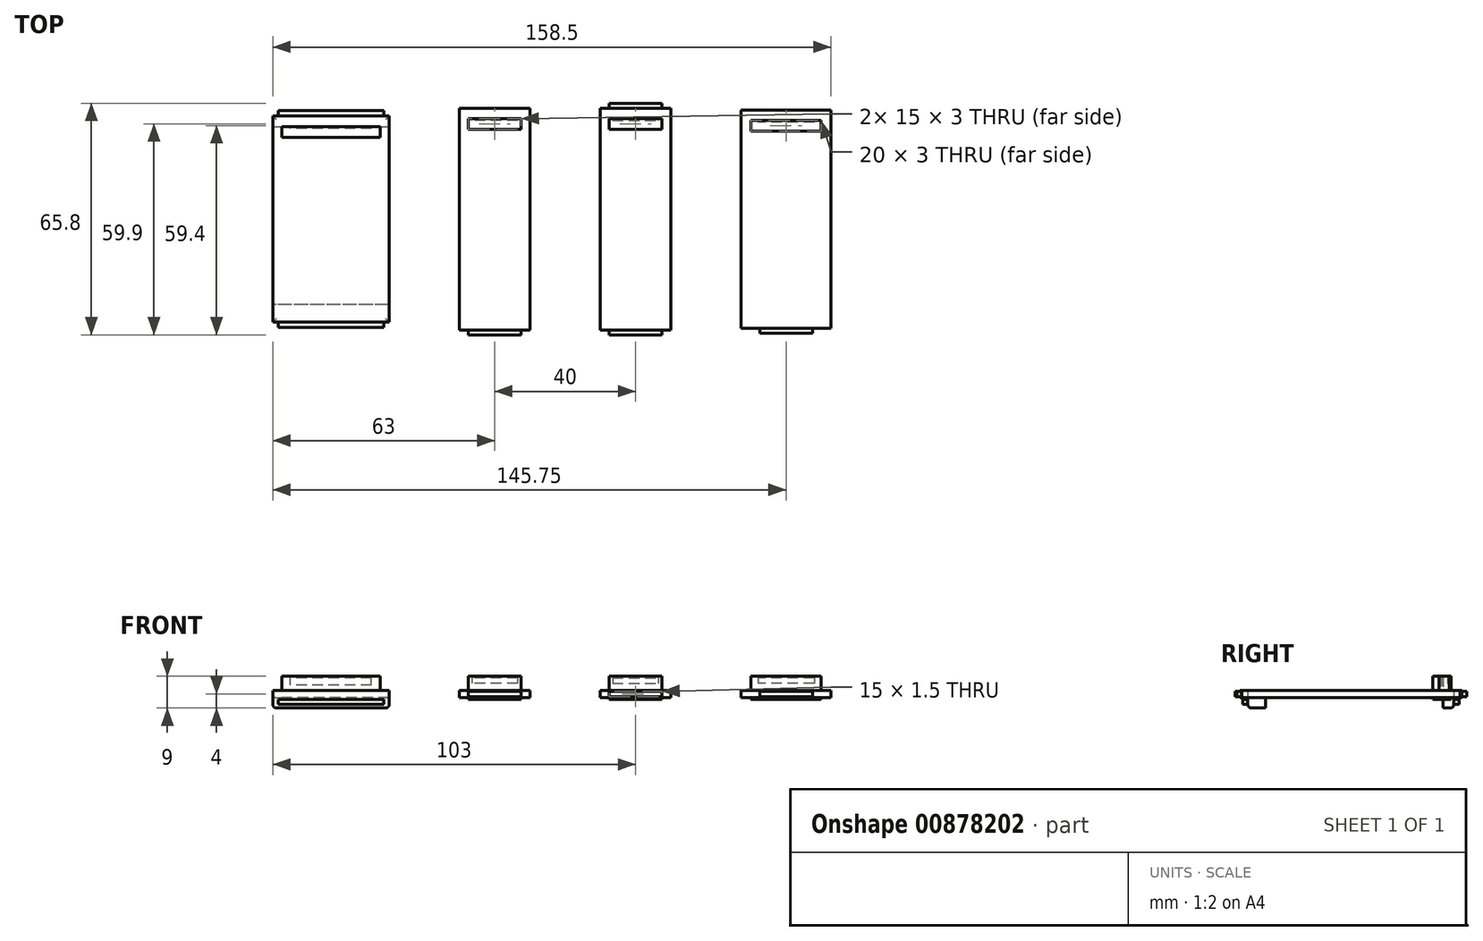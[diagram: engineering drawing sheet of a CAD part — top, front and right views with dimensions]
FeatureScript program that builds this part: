
annotation { "Feature Type Name" : "Feature", "Feature Type Description" : "" }
export const myFeature = defineFeature(function(context is Context, id is Id, definition is map)
    precondition{}
    {
        {
            var Q0;
            Q0=qCreatedBy(makeId("Top.planeOp"),FACE);
            var sketch = newSketch(context, id + "F0", { "sketchPlane" : qUnion([Q0])});
            skLineSegment(sketch, "E0.bottom", {"start": v(-83, 29.25) * mm, "end": v(-50, 29.25) * mm});
            skLineSegment(sketch, "E0.top", {"start": v(-83, -29.25) * mm, "end": v(-50, -29.25) * mm});
            skLineSegment(sketch, "E0.left", {"start": v(-83, 29.25) * mm, "end": v(-83, -29.25) * mm});
            skLineSegment(sketch, "E0.right", {"start": v(-50, 29.25) * mm, "end": v(-50, -29.25) * mm});
            skLineSegment(sketch, "E1.bottom", {"start": v(-30, 31.5) * mm, "end": v(-10, 31.5) * mm});
            skLineSegment(sketch, "E1.top", {"start": v(-30, -31.5) * mm, "end": v(-10, -31.5) * mm});
            skLineSegment(sketch, "E1.left", {"start": v(-30, 31.5) * mm, "end": v(-30, -31.5) * mm});
            skLineSegment(sketch, "E1.right", {"start": v(-10, 31.5) * mm, "end": v(-10, -31.5) * mm});
            skLineSegment(sketch, "E2.bottom", {"start": v(50, 31) * mm, "end": v(75.5, 31) * mm});
            skLineSegment(sketch, "E2.top", {"start": v(50, -31) * mm, "end": v(75.5, -31) * mm});
            skLineSegment(sketch, "E2.left", {"start": v(50, 31) * mm, "end": v(50, -31) * mm});
            skLineSegment(sketch, "E2.right", {"start": v(75.5, 31) * mm, "end": v(75.5, -31) * mm});
            skLineSegment(sketch, "E3.MirrorCS", {"start": v(10, 31.5) * mm, "end": v(10, -31.5) * mm});
            skLineSegment(sketch, "E4.MirrorCS", {"start": v(30, 31.5) * mm, "end": v(10, 31.5) * mm});
            skLineSegment(sketch, "E5.MirrorCS", {"start": v(30, 31.5) * mm, "end": v(30, -31.5) * mm});
            skLineSegment(sketch, "E6.MirrorCS", {"start": v(30, -31.5) * mm, "end": v(10, -31.5) * mm});
            skLineSegment(sketch, "E7", {"start": v(-66.5, 60.22) * mm, "end": v(-66.5, -59.01) * mm, "construction": true});
            skLineSegment(sketch, "E8", {"start": v(-20, 59.72) * mm, "end": v(-20, -67.05) * mm, "construction": true});
            skLineSegment(sketch, "E9.MirrorCS", {"start": v(20, 59.72) * mm, "end": v(20, -67.05) * mm, "construction": true});
            skLineSegment(sketch, "E10", {"start": v(62.75, 62.51) * mm, "end": v(62.75, -58.69) * mm, "construction": true});
            skLineSegment(sketch, "E11.MirrorCS", {"start": v(-76, -29.25) * mm, "end": v(-57, -29.25) * mm});
            skLineSegment(sketch, "E12.bottom", {"start": v(-27.5, 31.5) * mm, "end": v(-12.5, 31.5) * mm});
            skLineSegment(sketch, "E12.top", {"start": v(-27.5, 32.9) * mm, "end": v(-12.5, 32.9) * mm});
            skLineSegment(sketch, "E12.left", {"start": v(-27.5, 31.5) * mm, "end": v(-27.5, 32.9) * mm});
            skLineSegment(sketch, "E12.right", {"start": v(-12.5, 31.5) * mm, "end": v(-12.5, 32.9) * mm});
            skLineSegment(sketch, "E13.MirrorCS", {"start": v(27.5, 31.5) * mm, "end": v(12.5, 31.5) * mm});
            skLineSegment(sketch, "E14.MirrorCS", {"start": v(27.5, 31.5) * mm, "end": v(27.5, 32.9) * mm});
            skLineSegment(sketch, "E15.MirrorCS", {"start": v(12.5, 31.5) * mm, "end": v(12.5, 32.9) * mm});
            skLineSegment(sketch, "E16.MirrorCS", {"start": v(27.5, 32.9) * mm, "end": v(12.5, 32.9) * mm});
            skLineSegment(sketch, "E17.MirrorCS", {"start": v(10, -31.5) * mm, "end": v(10, 31.5) * mm});
            skLineSegment(sketch, "E18.MirrorCS", {"start": v(-12.5, -31.5) * mm, "end": v(-12.5, -32.9) * mm});
            skLineSegment(sketch, "E19.MirrorCS", {"start": v(-27.5, -31.5) * mm, "end": v(-27.5, -32.9) * mm});
            skLineSegment(sketch, "E20.MirrorCS", {"start": v(27.5, -31.5) * mm, "end": v(27.5, -32.9) * mm});
            skLineSegment(sketch, "E21.MirrorCS", {"start": v(-10, -31.5) * mm, "end": v(-10, 31.5) * mm});
            skLineSegment(sketch, "E22.MirrorCS", {"start": v(12.5, -31.5) * mm, "end": v(12.5, -32.9) * mm});
            skLineSegment(sketch, "E23.MirrorCS", {"start": v(-27.5, -31.5) * mm, "end": v(-12.5, -31.5) * mm});
            skLineSegment(sketch, "E24.MirrorCS", {"start": v(20, -59.72) * mm, "end": v(20, 67.05) * mm, "construction": true});
            skLineSegment(sketch, "E25.MirrorCS", {"start": v(27.5, -31.5) * mm, "end": v(12.5, -31.5) * mm});
            skLineSegment(sketch, "E26.MirrorCS", {"start": v(-27.5, -32.9) * mm, "end": v(-12.5, -32.9) * mm});
            skLineSegment(sketch, "E27.MirrorCS", {"start": v(27.5, -32.9) * mm, "end": v(12.5, -32.9) * mm});
            skLineSegment(sketch, "E28.MirrorCS", {"start": v(-20, -59.72) * mm, "end": v(-20, 67.05) * mm, "construction": true});
            skLineSegment(sketch, "E29.bottom", {"start": v(55.25, 31) * mm, "end": v(70.25, 31) * mm});
            skLineSegment(sketch, "E29.top", {"start": v(55.25, 32.4) * mm, "end": v(70.25, 32.4) * mm});
            skLineSegment(sketch, "E29.left", {"start": v(55.25, 31) * mm, "end": v(55.25, 32.4) * mm});
            skLineSegment(sketch, "E29.right", {"start": v(70.25, 31) * mm, "end": v(70.25, 32.4) * mm});
            skLineSegment(sketch, "E30.MirrorCS", {"start": v(55.25, -31) * mm, "end": v(70.25, -31) * mm});
            skLineSegment(sketch, "E31.MirrorCS", {"start": v(62.75, -62.51) * mm, "end": v(62.75, 58.69) * mm, "construction": true});
            skLineSegment(sketch, "E32.MirrorCS", {"start": v(55.25, -31) * mm, "end": v(55.25, -32.4) * mm});
            skLineSegment(sketch, "E33.MirrorCS", {"start": v(70.25, -31) * mm, "end": v(70.25, -32.4) * mm});
            skLineSegment(sketch, "E34.MirrorCS", {"start": v(55.25, -32.4) * mm, "end": v(70.25, -32.4) * mm});
            skLineSegment(sketch, "E35.bottom", {"start": v(-80.5, 26.25) * mm, "end": v(-52.5, 26.25) * mm});
            skLineSegment(sketch, "E35.top", {"start": v(-80.5, 23.25) * mm, "end": v(-52.5, 23.25) * mm});
            skLineSegment(sketch, "E35.left", {"start": v(-80.5, 26.25) * mm, "end": v(-80.5, 23.25) * mm});
            skLineSegment(sketch, "E35.right", {"start": v(-52.5, 26.25) * mm, "end": v(-52.5, 23.25) * mm});
            skLineSegment(sketch, "E36.bottom", {"start": v(-27.5, 28.5) * mm, "end": v(-12.5, 28.5) * mm});
            skLineSegment(sketch, "E36.top", {"start": v(-27.5, 25.5) * mm, "end": v(-12.5, 25.5) * mm});
            skLineSegment(sketch, "E36.left", {"start": v(-27.5, 28.5) * mm, "end": v(-27.5, 25.5) * mm});
            skLineSegment(sketch, "E36.right", {"start": v(-12.5, 28.5) * mm, "end": v(-12.5, 25.5) * mm});
            skLineSegment(sketch, "E37.MirrorCS", {"start": v(27.5, 28.5) * mm, "end": v(12.5, 28.5) * mm});
            skLineSegment(sketch, "E38.MirrorCS", {"start": v(12.5, 28.5) * mm, "end": v(12.5, 25.5) * mm});
            skLineSegment(sketch, "E39.MirrorCS", {"start": v(27.5, 28.5) * mm, "end": v(27.5, 25.5) * mm});
            skLineSegment(sketch, "E40.MirrorCS", {"start": v(27.5, 25.5) * mm, "end": v(12.5, 25.5) * mm});
            skLineSegment(sketch, "E41.bottom", {"start": v(52.75, 28) * mm, "end": v(72.75, 28) * mm});
            skLineSegment(sketch, "E41.top", {"start": v(52.75, 25) * mm, "end": v(72.75, 25) * mm});
            skLineSegment(sketch, "E41.left", {"start": v(52.75, 28) * mm, "end": v(52.75, 25) * mm});
            skLineSegment(sketch, "E41.right", {"start": v(72.75, 28) * mm, "end": v(72.75, 25) * mm});
            skSolve(sketch);
        }
        {
            var Q0;
            Q0=makeQuery(id+"F0.imprint","IMPRINT",FACE,{"disambiguationData":[TD([[makeQuery(id+"F0.imprint","IMPRINT",EDGE,{"derivedFrom":sQuery(id+"F0.wireOp",EDGE,"icYe6frA-JgaZ-y4PL-hhxq-wq9PyiB64fKO.bottom")}),1.0]])]});
            var Q1;
            Q1=makeQuery(id+"F0.imprint","IMPRINT",FACE,{"disambiguationData":[TD([[makeQuery(id+"F0.imprint","IMPRINT",EDGE,{"derivedFrom":sQuery(id+"F0.wireOp",EDGE,"E12.bottom")}),1.0]])]});
            var Q2;
            {var subQ0=sQuery(id+"F0.wireOp",EDGE,"E14.MirrorCS");Q2=makeQuery(id+"F0.imprint","IMPRINT",FACE,{"disambiguationData":[TD([[makeQuery(id+"F0.imprint","IMPRINT",EDGE,{"derivedFrom":subQ0}),1.0]])]});}
            var Q3;
            Q3=makeQuery(id+"F0.imprint","IMPRINT",FACE,{"disambiguationData":[TD([[makeQuery(id+"F0.imprint","IMPRINT",EDGE,{"derivedFrom":sQuery(id+"F0.wireOp",EDGE,"E29.bottom")}),1.0]])]});
            var Q4;
            {var subQ0=sQuery(id+"F0.wireOp",EDGE,"E32.MirrorCS");Q4=makeQuery(id+"F0.imprint","IMPRINT",FACE,{"disambiguationData":[TD([[makeQuery(id+"F0.imprint","IMPRINT",EDGE,{"derivedFrom":subQ0}),1.0]])]});}
            var Q5;
            Q5=makeQuery(id+"F0.imprint","IMPRINT",FACE,{"disambiguationData":[TD([[makeQuery(id+"F0.imprint","IMPRINT",EDGE,{"derivedFrom":sQuery(id+"F0.wireOp",EDGE,"E20.MirrorCS")}),-1.0]])]});
            var Q6;
            {var subQ0=sQuery(id+"F0.wireOp",EDGE,"E18.MirrorCS");Q6=makeQuery(id+"F0.imprint","IMPRINT",FACE,{"disambiguationData":[TD([[makeQuery(id+"F0.imprint","IMPRINT",EDGE,{"derivedFrom":subQ0}),-1.0]])]});}
            var Q7;
            Q7=makeQuery(id+"F0.imprint","IMPRINT",FACE,{"disambiguationData":[TD([[makeQuery(id+"F0.imprint","IMPRINT",EDGE,{"derivedFrom":sQuery(id+"F0.wireOp",EDGE,"26aa9f08-f274-459f-a98e-a8d90b5829f30.MirrorCS")}),-1.0]])]});
            extrude(context, id + "F1", {"entities" : qUnion([Q0, Q1, Q2, Q3, Q4, Q5, Q6, Q7]), "endBound" : BoundingType.SYMMETRIC, "depth" : 1.5 * mm, "offsetDistance" : 25 * mm});
        }
        {
            var Q0;
            {var subQ4=sQuery(id+"F0.wireOp",EDGE,"E0.left");Q0=makeQuery(id+"F0.imprint","IMPRINT",FACE,{"disambiguationData":[TD([[makeQuery(id+"F0.imprint","IMPRINT",EDGE,{"derivedFrom":subQ4}),1.0]])]});}
            var Q1;
            {var subQ0=sQuery(id+"F0.wireOp",EDGE,"E1.left");Q1=makeQuery(id+"F0.imprint","IMPRINT",FACE,{"disambiguationData":[TD([[makeQuery(id+"F0.imprint","IMPRINT",EDGE,{"derivedFrom":subQ0}),1.0]])]});}
            var Q2;
            {var subQ4=sQuery(id+"F0.wireOp",EDGE,"E5.MirrorCS");Q2=makeQuery(id+"F0.imprint","IMPRINT",FACE,{"disambiguationData":[TD([[makeQuery(id+"F0.imprint","IMPRINT",EDGE,{"derivedFrom":subQ4}),-1.0]])]});}
            var Q3;
            {var subQ1=sQuery(id+"F0.wireOp",EDGE,"E2.left");Q3=makeQuery(id+"F0.imprint","IMPRINT",FACE,{"disambiguationData":[TD([[makeQuery(id+"F0.imprint","IMPRINT",EDGE,{"derivedFrom":subQ1}),1.0]])]});}
            extrude(context, id + "F2", {"entities" : qUnion([Q0, Q1, Q2, Q3]), "operationType" : NewBodyOperationType.ADD, "endBound" : BoundingType.SYMMETRIC, "depth" : 2 * mm, "offsetDistance" : 25 * mm});
        }
        {
            var Q0;
            Q0=makeQuery(id+"F0.imprint","IMPRINT",FACE,{"disambiguationData":[TD([[makeQuery(id+"F0.imprint","IMPRINT",EDGE,{"derivedFrom":sQuery(id+"F0.wireOp",EDGE,"E35.bottom")}),-1.0]])]});
            var Q1;
            Q1=makeQuery(id+"F0.imprint","IMPRINT",FACE,{"disambiguationData":[TD([[makeQuery(id+"F0.imprint","IMPRINT",EDGE,{"derivedFrom":sQuery(id+"F0.wireOp",EDGE,"E36.bottom")}),-1.0]])]});
            var Q2;
            Q2=makeQuery(id+"F0.imprint","IMPRINT",FACE,{"disambiguationData":[TD([[makeQuery(id+"F0.imprint","IMPRINT",EDGE,{"derivedFrom":sQuery(id+"F0.wireOp",EDGE,"E37.MirrorCS")}),1.0]])]});
            var Q3;
            Q3=makeQuery(id+"F0.imprint","IMPRINT",FACE,{"disambiguationData":[TD([[makeQuery(id+"F0.imprint","IMPRINT",EDGE,{"derivedFrom":sQuery(id+"F0.wireOp",EDGE,"E41.bottom")}),-1.0]])]});
            extrude(context, id + "F3", {"entities" : qUnion([Q0, Q1, Q2, Q3]), "operationType" : NewBodyOperationType.ADD, "depth" : 5 * mm, "offsetDistance" : 25 * mm, "hasSecondDirection" : true, "secondDirectionOppositeDirection" : true, "secondDirectionDepth" : 1.5 * mm});
        }
        {
            var Q0;
            Q0=makeQuery(id+"F3.opExtrude","SWEPT_FACE",FACE,{"disambiguationData":[OSD([sQuery(id+"F0.wireOp",EDGE,"E35.bottom")])]});
            var sketch = newSketch(context, id + "F4", { "sketchPlane" : qUnion([Q0])});
            skLineSegment(sketch, "E42.bottom", {"start": v(55, 2.5) * mm, "end": v(78, 2.5) * mm});
            skLineSegment(sketch, "E42.top", {"start": v(55, 4.5) * mm, "end": v(78, 4.5) * mm});
            skLineSegment(sketch, "E42.left", {"start": v(55, 2.5) * mm, "end": v(55, 4.5) * mm});
            skLineSegment(sketch, "E42.right", {"start": v(78, 2.5) * mm, "end": v(78, 4.5) * mm});
            skSolve(sketch);
        }
        {
            var Q0;
            Q0=makeQuery(id+"F4.imprint","IMPRINT",FACE,{"disambiguationData":[TD([[makeQuery(id+"F4.imprint","IMPRINT",EDGE,{"derivedFrom":sQuery(id+"F4.wireOp",EDGE,"E42.bottom")}),1.0]])]});
            extrude(context, id + "F5", {"entities" : qUnion([Q0]), "operationType" : NewBodyOperationType.REMOVE, "oppositeDirection" : true, "depth" : 0.5 * mm, "offsetDistance" : 25 * mm});
        }
        {
            var Q0;
            Q0=makeQuery(id+"F3.opExtrude","SWEPT_FACE",FACE,{"disambiguationData":[OSD([sQuery(id+"F0.wireOp",EDGE,"E36.bottom")])]});
            var sketch = newSketch(context, id + "F6", { "sketchPlane" : qUnion([Q0])});
            skLineSegment(sketch, "E43.bottom", {"start": v(13.5, 4.5) * mm, "end": v(26.5, 4.5) * mm});
            skLineSegment(sketch, "E43.top", {"start": v(13.5, 3) * mm, "end": v(26.5, 3) * mm});
            skLineSegment(sketch, "E43.left", {"start": v(13.5, 4.5) * mm, "end": v(13.5, 3) * mm});
            skLineSegment(sketch, "E43.right", {"start": v(26.5, 4.5) * mm, "end": v(26.5, 3) * mm});
            skLineSegment(sketch, "E44.MirrorCS", {"start": v(-26.5, 4.5) * mm, "end": v(-26.5, 3) * mm});
            skLineSegment(sketch, "E45.MirrorCS", {"start": v(-13.5, 4.5) * mm, "end": v(-13.5, 3) * mm});
            skLineSegment(sketch, "E46.MirrorCS", {"start": v(-13.5, 4.5) * mm, "end": v(-26.5, 4.5) * mm});
            skLineSegment(sketch, "E47.MirrorCS", {"start": v(-13.5, 3) * mm, "end": v(-26.5, 3) * mm});
            skSolve(sketch);
        }
        {
            var Q0;
            Q0=makeQuery(id+"F6.imprint","IMPRINT",FACE,{"disambiguationData":[TD([[makeQuery(id+"F6.imprint","IMPRINT",EDGE,{"derivedFrom":sQuery(id+"F6.wireOp",EDGE,"E44.MirrorCS")}),1.0]])]});
            var Q1;
            Q1=makeQuery(id+"F6.imprint","IMPRINT",FACE,{"disambiguationData":[TD([[makeQuery(id+"F6.imprint","IMPRINT",EDGE,{"derivedFrom":sQuery(id+"F6.wireOp",EDGE,"E43.bottom")}),-1.0]])]});
            extrude(context, id + "F7", {"entities" : qUnion([Q0, Q1]), "operationType" : NewBodyOperationType.REMOVE, "oppositeDirection" : true, "depth" : 0.5 * mm, "offsetDistance" : 25 * mm});
        }
        {
            var Q0;
            Q0=makeQuery(id+"F3.opExtrude","SWEPT_FACE",FACE,{"disambiguationData":[OSD([sQuery(id+"F0.wireOp",EDGE,"E41.bottom")])]});
            var sketch = newSketch(context, id + "F8", { "sketchPlane" : qUnion([Q0])});
            skLineSegment(sketch, "E48.bottom", {"start": v(-70.75, 4.5) * mm, "end": v(-54.75, 4.5) * mm});
            skLineSegment(sketch, "E48.top", {"start": v(-70.75, 3) * mm, "end": v(-54.75, 3) * mm});
            skLineSegment(sketch, "E48.left", {"start": v(-70.75, 4.5) * mm, "end": v(-70.75, 3) * mm});
            skLineSegment(sketch, "E48.right", {"start": v(-54.75, 4.5) * mm, "end": v(-54.75, 3) * mm});
            skSolve(sketch);
        }
        {
            var Q0;
            Q0=makeQuery(id+"F8.imprint","IMPRINT",FACE,{"disambiguationData":[TD([[makeQuery(id+"F8.imprint","IMPRINT",EDGE,{"derivedFrom":sQuery(id+"F8.wireOp",EDGE,"E48.bottom")}),-1.0]])]});
            extrude(context, id + "F9", {"entities" : qUnion([Q0]), "operationType" : NewBodyOperationType.REMOVE, "oppositeDirection" : true, "depth" : 0.5 * mm, "offsetDistance" : 25 * mm});
        }
        {
            var Q0;
            {var subQ0=sQuery(id+"F0.wireOp",EDGE,"E35.right");var subQ1=sQuery(id+"F0.wireOp",EDGE,"E35.left");var subQ2=sQuery(id+"F0.wireOp",EDGE,"E35.top");var subQ3=sQuery(id+"F0.wireOp",EDGE,"E35.bottom");Q0=makeQuery(id+"F3.boolean.opBoolean","MERGE",FACE,{"derivedFrom":[makeQuery(id+"F2.opExtrude","CAP_FACE",FACE,{"disambiguationData":[OSD([sQuery(id+"F0.wireOp",EDGE,"E0.bottom"),sQuery(id+"F0.wireOp",EDGE,"E0.top"),sQuery(id+"F0.wireOp",EDGE,"E0.left"),sQuery(id+"F0.wireOp",EDGE,"E0.right"),sQuery(id+"F0.wireOp",EDGE,"E11.MirrorCS"),subQ3,subQ2,subQ1,subQ0])],"isStart":true}),makeQuery(id+"F3.opExtrude","CAP_FACE",FACE,{"disambiguationData":[OSD([subQ3,subQ2,subQ1,subQ0])],"isStart":true})]});}
            var sketch = newSketch(context, id + "F10", { "sketchPlane" : qUnion([Q0])});
            skLineSegment(sketch, "E49.bottom", {"start": v(-83, -29.25) * mm, "end": v(-50, -29.25) * mm});
            skLineSegment(sketch, "E49.top", {"start": v(-83, -26.25) * mm, "end": v(-50, -26.25) * mm});
            skLineSegment(sketch, "E49.left", {"start": v(-83, -29.25) * mm, "end": v(-83, -26.25) * mm});
            skLineSegment(sketch, "E49.right", {"start": v(-50, -29.25) * mm, "end": v(-50, -26.25) * mm});
            skLineSegment(sketch, "E50.MirrorCS", {"start": v(-83, 29.25) * mm, "end": v(-50, 29.25) * mm});
            skLineSegment(sketch, "E51.MirrorCS", {"start": v(-50, 29.25) * mm, "end": v(-50, 24.25) * mm});
            skLineSegment(sketch, "E52", {"start": v(-50, 24.25) * mm, "end": v(-83, 24.25) * mm});
            skLineSegment(sketch, "E53", {"start": v(-83, 29.25) * mm, "end": v(-83, 24.25) * mm});
            skSolve(sketch);
        }
        {
            var Q0;
            Q0=makeQuery(id+"F10.imprint","IMPRINT",FACE,{"disambiguationData":[TD([[makeQuery(id+"F10.imprint","IMPRINT",EDGE,{"derivedFrom":sQuery(id+"F10.wireOp",EDGE,"E49.bottom")}),1.0]])]});
            var Q1;
            Q1=makeQuery(id+"F10.imprint","IMPRINT",FACE,{"disambiguationData":[TD([[makeQuery(id+"F10.imprint","IMPRINT",EDGE,{"derivedFrom":sQuery(id+"F10.wireOp",EDGE,"ca0315dc-eba7-49f8-a230-0cf44bd582940.MirrorCS")}),-1.0]])]});
            var Q2;
            Q2=makeQuery(id+"F10.imprint","IMPRINT",FACE,{"disambiguationData":[TD([[makeQuery(id+"F10.imprint","IMPRINT",EDGE,{"derivedFrom":sQuery(id+"F10.wireOp",EDGE,"E50.MirrorCS")}),-1.0]])]});
            extrude(context, id + "F11", {"entities" : qUnion([Q0, Q1, Q2]), "operationType" : NewBodyOperationType.ADD, "depth" : 3 * mm, "offsetDistance" : 25 * mm});
        }
        {
            var Q0;
            Q0=makeQuery(id+"F11.boolean.opBoolean","MERGE",FACE,{"derivedFrom":[makeQuery(id+"F2.opExtrude","SWEPT_FACE",FACE,{"disambiguationData":[OSD([sQuery(id+"F0.wireOp",EDGE,"E0.bottom")])]}),makeQuery(id+"F11.opExtrude","SWEPT_FACE",FACE,{"disambiguationData":[OSD([sQuery(id+"F10.wireOp",EDGE,"E49.bottom")])]})]});
            var sketch = newSketch(context, id + "F12", { "sketchPlane" : qUnion([Q0])});
            skLineSegment(sketch, "E54.bottom", {"start": v(51.5, -1.5) * mm, "end": v(81.5, -1.5) * mm});
            skLineSegment(sketch, "E54.top", {"start": v(51.5, -3) * mm, "end": v(81.5, -3) * mm});
            skLineSegment(sketch, "E54.left", {"start": v(51.5, -1.5) * mm, "end": v(51.5, -3) * mm});
            skLineSegment(sketch, "E54.right", {"start": v(81.5, -1.5) * mm, "end": v(81.5, -3) * mm});
            skSolve(sketch);
        }
        {
            var Q0;
            Q0=makeQuery(id+"F12.imprint","IMPRINT",FACE,{"disambiguationData":[TD([[makeQuery(id+"F12.imprint","IMPRINT",EDGE,{"derivedFrom":sQuery(id+"F12.wireOp",EDGE,"E54.bottom")}),-1.0]])]});
            extrude(context, id + "F13", {"entities" : qUnion([Q0]), "operationType" : NewBodyOperationType.ADD, "depth" : 1.5 * mm, "offsetDistance" : 25 * mm});
        }
        {
            var Q0;
            Q0=makeQuery(id+"F11.boolean.opBoolean","MERGE",FACE,{"derivedFrom":[makeQuery(id+"F2.opExtrude","SWEPT_FACE",FACE,{"disambiguationData":[OSD([sQuery(id+"F0.wireOp",EDGE,"E0.top"),sQuery(id+"F0.wireOp",EDGE,"E11.MirrorCS")])]}),makeQuery(id+"F11.opExtrude","SWEPT_FACE",FACE,{"disambiguationData":[OSD([sQuery(id+"F10.wireOp",EDGE,"E50.MirrorCS")])]})]});
            var sketch = newSketch(context, id + "F14", { "sketchPlane" : qUnion([Q0])});
            skLineSegment(sketch, "E55.0", {"start": v(-51.5, -1.5) * mm, "end": v(-81.5, -1.5) * mm});
            skLineSegment(sketch, "E56.0", {"start": v(-81.5, -1.5) * mm, "end": v(-81.5, -3) * mm});
            skLineSegment(sketch, "E57.0", {"start": v(-51.5, -3) * mm, "end": v(-81.5, -3) * mm});
            skLineSegment(sketch, "E58.0", {"start": v(-51.5, -1.5) * mm, "end": v(-51.5, -3) * mm});
            skSolve(sketch);
        }
        {
            var Q0;
            Q0=makeQuery(id+"F14.imprint","IMPRINT",FACE,{"disambiguationData":[TD([[makeQuery(id+"F14.imprint","IMPRINT",EDGE,{"derivedFrom":sQuery(id+"F14.wireOp",EDGE,"E55.0")}),1.0]])]});
            extrude(context, id + "F15", {"entities" : qUnion([Q0]), "operationType" : NewBodyOperationType.ADD, "depth" : 1.5 * mm, "offsetDistance" : 25 * mm});
        }
        {
            var Q0;
            Q0=makeQuery(id+"F11.opExtrude","CAP_EDGE",EDGE,{"disambiguationData":[OSD([sQuery(id+"F10.wireOp",EDGE,"E49.bottom")])],"isStart":false});
            var Q1;
            Q1=makeQuery(id+"F11.opExtrude","CAP_EDGE",EDGE,{"disambiguationData":[OSD([sQuery(id+"F10.wireOp",EDGE,"E50.MirrorCS")])],"isStart":false});
            var Q2;
            Q2=makeQuery(id+"F11.opExtrude","CAP_EDGE",EDGE,{"disambiguationData":[OSD([sQuery(id+"F10.wireOp",EDGE,"E49.left")])],"isStart":false});
            var Q3;
            Q3=makeQuery(id+"F11.opExtrude","CAP_EDGE",EDGE,{"disambiguationData":[OSD([sQuery(id+"F10.wireOp",EDGE,"E53")])],"isStart":false});
            var Q4;
            Q4=makeQuery(id+"F11.opExtrude","CAP_EDGE",EDGE,{"disambiguationData":[OSD([sQuery(id+"F10.wireOp",EDGE,"E49.right")])],"isStart":false});
            var Q5;
            Q5=makeQuery(id+"F11.opExtrude","CAP_EDGE",EDGE,{"disambiguationData":[OSD([sQuery(id+"F10.wireOp",EDGE,"E51.MirrorCS")])],"isStart":false});
            fillet(context, id + "F16", {"entities" : qUnion([Q0, Q1, Q2, Q3, Q4, Q5]), "radius" : 1 * mm, "tangentPropagation" : true, "allowEdgeOverflow" : false});
        }
    });
